# Revit family: 1301A_OMNIDT_Cutsheet
name_source: partatom
category: Communication Devices
units: mm (PartAtom-declared; Revit-internal decimal feet)

## family parameters
Cut with Voids When Loaded = No
Host = Face
Maintain Annotation Orientation = No
OmniClass Number = 23.85.80.11.27
OmniClass Title = Lighting Controls
Part Type = Normal
Room Calculation Point = No
Round Connector Dimension = Use Diameter
Shared = Yes

## types (1)
- 1301A_OMNIDT_Cutsheet
    Assembly Code = D5090
    Certifications = UL and cUL listed
    Coverage = 500 - 2000 sq ft, based on model
    Default Elevation = 48 "
    Description = The OMNI DT combines ultrasonic (US) and passive infrared (PIR) technologies
to turn lighting on and off based on occupancy. This dual technology provides
accurate turn-ons while virtually eliminating false-offs. This sensor features
 Controls' patented IntelliDAPT® technology, which makes all the sensor
adjustments automatically
    Features = IntelliDAPT self-adaptive technology - no manual adjustment required
• All-digital dual technology (ultrasonic [US] and
passive infrared [PIR]) sensor
• Non-volatile memory for sensor settings
• 500–2,000 square-foot coverage area (depending on model)
• Optional relay and photocell control
• Optional Quick to Install (QTI) connector
• UL and cUL listed
• California Title 24 compliant
• Five-year limited warranty
• Low Voltage 24 Vdc
    Housing Material = Paint - Matte White
    Manufacturer = NX Lighting Controls
    Model = NX Ceiling Mount Occupancy Sensors employ Passive Infrared
and Ultrasonic sensing technologies to turn lighting on and off based
on occupancy
    Power Requirements = 24VDC, 33mA (uses UVPP and MP- Series power pack- not included)
    Sensing Element = Metal-Nickel
    Type Comments = OMNI® Low Voltage Dual Technology Ultrasonic and PIR
    URL = https://www.currentlighting.com
    Warranty = 5-Years Warranty
    Width = 4.5 "

## geometry (parser evidence)
native form markers: Sweep x2
no freeform markers — native parametric forms only
